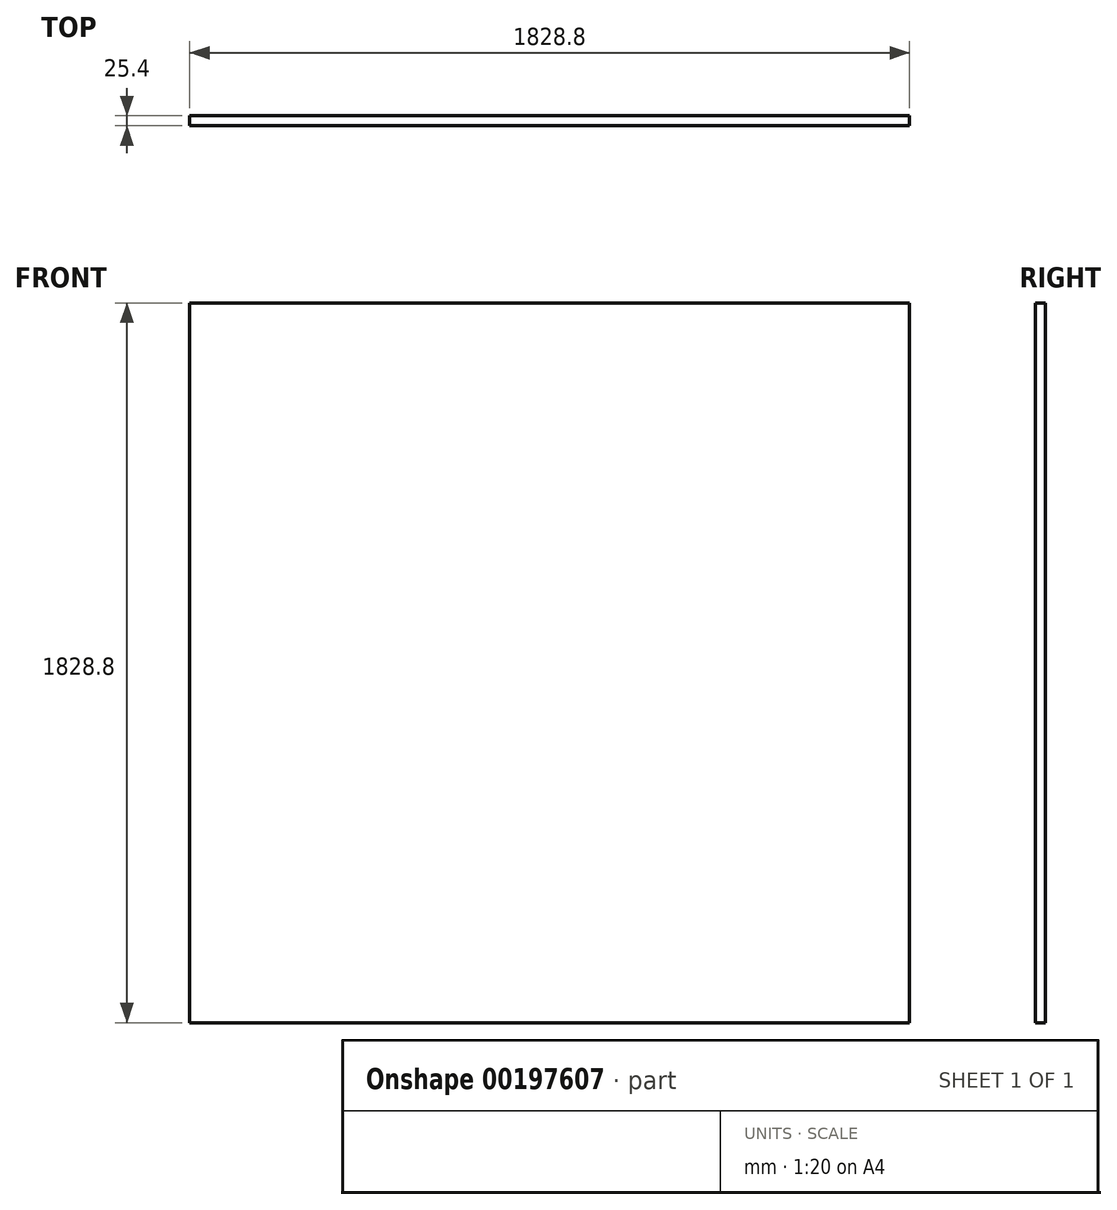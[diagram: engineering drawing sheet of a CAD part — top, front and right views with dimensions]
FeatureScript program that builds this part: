
annotation { "Feature Type Name" : "Feature", "Feature Type Description" : "" }
export const myFeature = defineFeature(function(context is Context, id is Id, definition is map)
    precondition{}
    {
        {
            var Q0;
            Q0=qCreatedBy(makeId("Front.planeOp"),FACE);
            var sketch = newSketch(context, id + "F0", { "sketchPlane" : qUnion([Q0])});
            skLineSegment(sketch, "E0.bottom", {"start": v(-913.17, 1054) * mm, "end": v(915.63, 1054) * mm});
            skLineSegment(sketch, "E0.top", {"start": v(-913.17, -774.8) * mm, "end": v(915.63, -774.8) * mm});
            skLineSegment(sketch, "E0.left", {"start": v(-913.17, 1054) * mm, "end": v(-913.17, -774.8) * mm});
            skLineSegment(sketch, "E0.right", {"start": v(915.63, 1054) * mm, "end": v(915.63, -774.8) * mm});
            skSolve(sketch);
        }
        {
            var Q0;
            Q0=makeQuery(id+"F0.imprint","IMPRINT",FACE,{"disambiguationData":[TD([[makeQuery(id+"F0.imprint","IMPRINT",EDGE,{"derivedFrom":sQuery(id+"F0.wireOp",EDGE,"E0.bottom")}),-1.0]])]});
            extrude(context, id + "F1", {"entities" : qUnion([Q0]), "depth" : 25.4 * mm});
        }
    });
